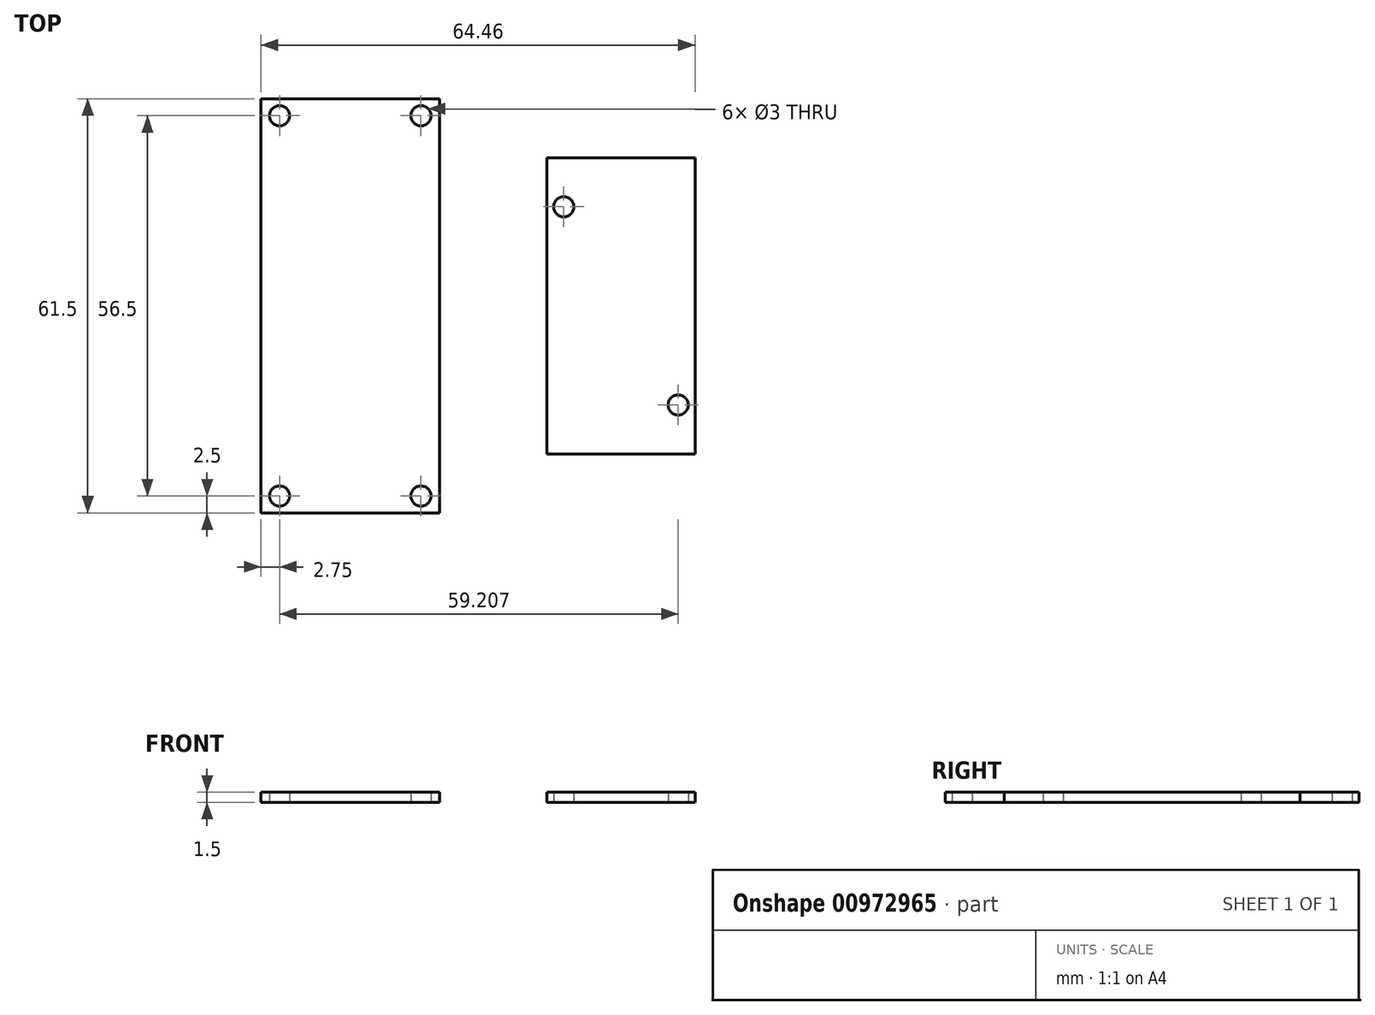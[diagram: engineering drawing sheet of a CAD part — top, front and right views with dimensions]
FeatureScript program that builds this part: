
annotation { "Feature Type Name" : "Feature", "Feature Type Description" : "" }
export const myFeature = defineFeature(function(context is Context, id is Id, definition is map)
    precondition{}
    {
        {
            var Q0;
            Q0=qCreatedBy(makeId("Top.planeOp"),FACE);
            var sketch = newSketch(context, id + "F0", { "sketchPlane" : qUnion([Q0])});
            skLineSegment(sketch, "E0.bottom", {"start": v(13.25, -30.75) * mm, "end": v(-13.25, -30.75) * mm});
            skLineSegment(sketch, "E0.top", {"start": v(13.25, 30.75) * mm, "end": v(-13.25, 30.75) * mm});
            skLineSegment(sketch, "E0.left", {"start": v(13.25, -30.75) * mm, "end": v(13.25, 30.75) * mm});
            skLineSegment(sketch, "E0.right", {"start": v(-13.25, -30.75) * mm, "end": v(-13.25, 30.75) * mm});
            skPoint(sketch, "E1.middle", {"position": v(0, 0) * mm});
            skCircle(sketch, "E2", {"center": v(10.5, 28.25) * mm, "radius": 1.5 * mm});
            skCircle(sketch, "E3", {"center": v(10.5, -28.25) * mm, "radius": 1.5 * mm});
            skCircle(sketch, "E4", {"center": v(-10.5, -28.25) * mm, "radius": 1.5 * mm});
            skCircle(sketch, "E5", {"center": v(-10.5, 28.25) * mm, "radius": 1.5 * mm});
            skLineSegment(sketch, "E6.bottom", {"start": v(10.5, -28.25) * mm, "end": v(-10.5, -28.25) * mm, "construction": true});
            skLineSegment(sketch, "E6.top", {"start": v(10.5, 28.25) * mm, "end": v(-10.5, 28.25) * mm, "construction": true});
            skLineSegment(sketch, "E6.left", {"start": v(10.5, -28.25) * mm, "end": v(10.5, 28.25) * mm, "construction": true});
            skLineSegment(sketch, "E6.right", {"start": v(-10.5, -28.25) * mm, "end": v(-10.5, 28.25) * mm, "construction": true});
            skSolve(sketch);
        }
        {
            var Q0;
            Q0=qSketchRegion(id+"F0",true);
            extrude(context, id + "F1", {"entities" : qUnion([Q0]), "depth" : 1.5 * mm, "offsetDistance" : 25 * mm});
        }
        {
            var Q0;
            Q0=qCreatedBy(makeId("Top.planeOp"),FACE);
            var sketch = newSketch(context, id + "F2", { "sketchPlane" : qUnion([Q0])});
            skLineSegment(sketch, "E7.bottom", {"start": v(51.2, 22) * mm, "end": v(29.2, 22) * mm});
            skLineSegment(sketch, "E7.top", {"start": v(51.2, -22) * mm, "end": v(29.2, -22) * mm});
            skLineSegment(sketch, "E7.left", {"start": v(51.2, 22) * mm, "end": v(51.2, -22) * mm});
            skLineSegment(sketch, "E7.right", {"start": v(29.2, 22) * mm, "end": v(29.2, -22) * mm});
            skPoint(sketch, "E7.middle", {"position": v(40.2, 0) * mm});
            skLineSegment(sketch, "E8", {"start": v(48.7, -14.72) * mm, "end": v(31.7, 14.72) * mm, "construction": true});
            skCircle(sketch, "E9", {"center": v(31.7, 14.72) * mm, "radius": 1.5 * mm});
            skCircle(sketch, "E10", {"center": v(48.7, -14.72) * mm, "radius": 1.5 * mm});
            skSolve(sketch);
        }
        {
            var Q0;
            Q0 = qSketchRegion(id + "F2", true);
            extrude(context, id + "F3", {"entities" : qUnion([Q0]), "depth" : 1.5 * mm, "offsetDistance" : 25 * mm});
        }
    });
